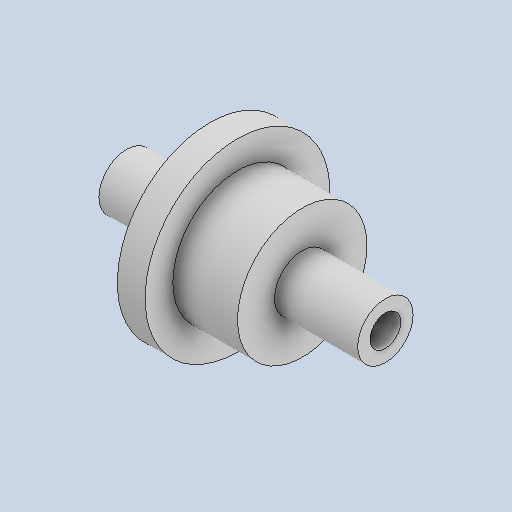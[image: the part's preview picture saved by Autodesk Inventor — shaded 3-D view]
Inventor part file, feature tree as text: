
AUTODESK INVENTOR PART (.ipt)
format: ipt  version: 2022 (Build 260153000, 153)  size: 147,456 bytes
history: native  units: mm
features: sketch x4, extrude x3, hole x1, mirror x1, plane x1
ambient origin geometry x8: Origin, YZ Plane, XZ Plane, XY Plane, X Axis, Y Axis, Z Axis, Center Point
bodies: Solid1 (feature_tree)
feature tree (10):
  extrude  "Extrusion1"  Depth=42.0mm TaperAngle=0.0deg
  hole  "Hole1"  [1 undecoded]
  mirror  "Mirror1"
  plane  "Work Plane2"
  extrude  "Extrusion2"  Depth=21.0mm
  extrude  "Extrusion3"  [1 undecoded]
  sketch  "Sketch1"  dims[d0=9.0mm d1=42.0mm d2=0.0mm]
  sketch  "Sketch2"  dims[d3=5.0mm d4=6.0mm d5=4.0mm d6=2.0mm d7=90.0deg d8=7.0mm d9=20.594885mm d10=30.0mm]
  sketch  "Sketch3"  dims[d11=4.5mm d12=0.0mm d13=21.0mm]
  sketch  "Sketch4"  dims[d15=0.0mm d17=-7.5mm d14=0.25mm d16=14.3117mm d18=20.594885mm d19=0.0625mm d20=0.75mm d21=0.375mm]
note: 2 required parameter values undecoded (feature->parameter linkage not recoverable at this tier; creation-order binding heuristic only, values carry confidence <= 0.55)
